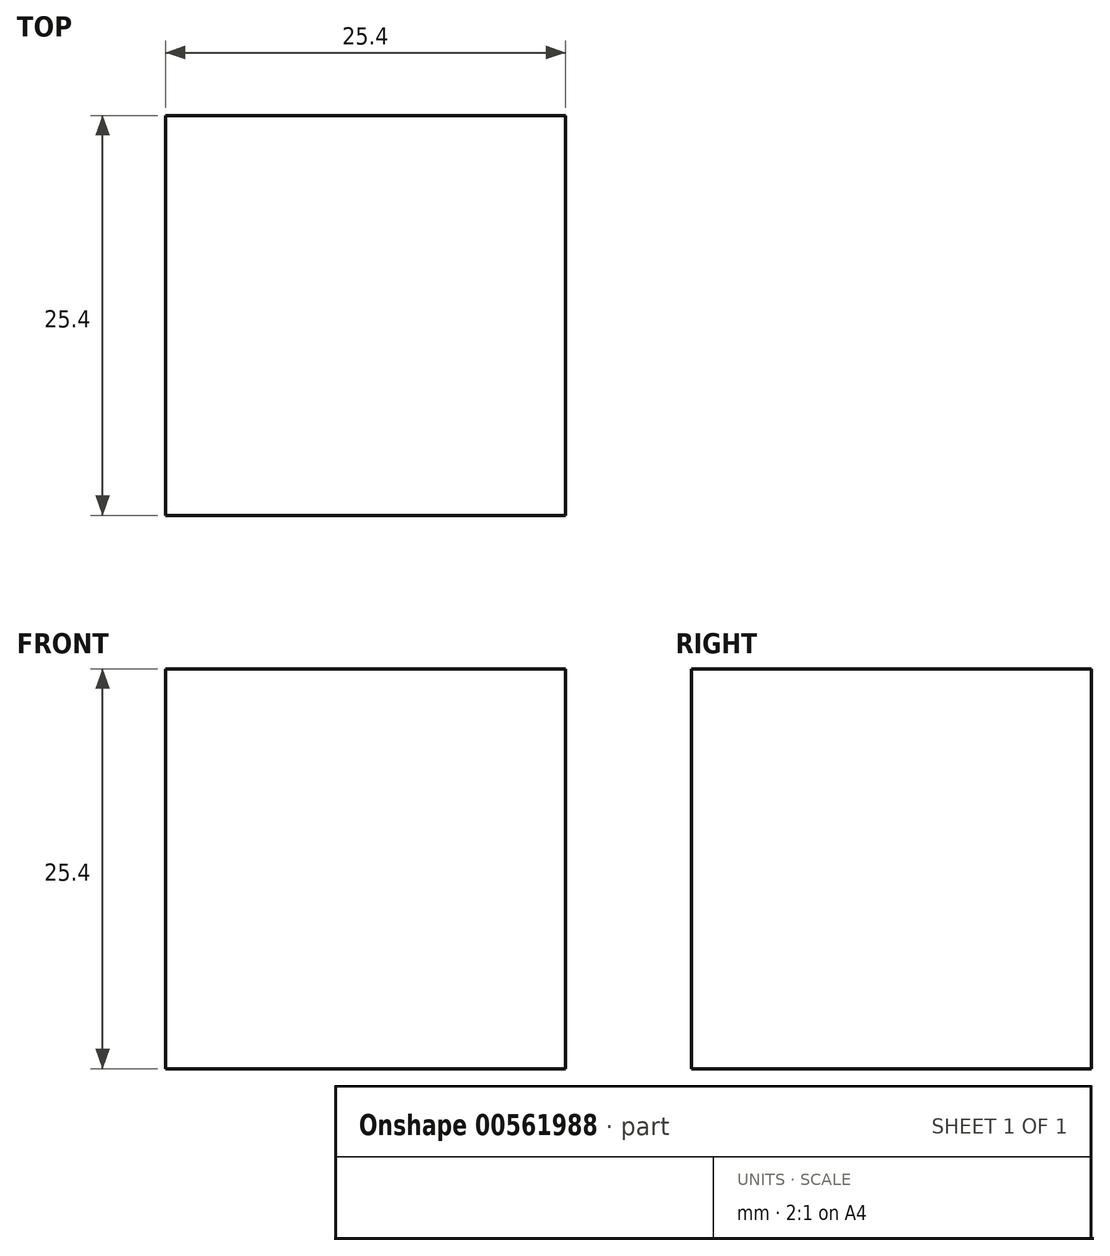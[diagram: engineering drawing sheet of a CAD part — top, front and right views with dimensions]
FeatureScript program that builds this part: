
annotation { "Feature Type Name" : "Feature", "Feature Type Description" : "" }
export const myFeature = defineFeature(function(context is Context, id is Id, definition is map)
    precondition{}
    {
        {
            var Q0;
            Q0=qCreatedBy(makeId("Front.planeOp"),FACE);
            var sketch = newSketch(context, id + "F0", { "sketchPlane" : qUnion([Q0])});
            skLineSegment(sketch, "E0.bottom", {"start": v(-72.33, 30.5) * mm, "end": v(-46.93, 30.5) * mm});
            skLineSegment(sketch, "E0.top", {"start": v(-72.33, 5.1) * mm, "end": v(-46.93, 5.1) * mm});
            skLineSegment(sketch, "E0.left", {"start": v(-72.33, 30.5) * mm, "end": v(-72.33, 5.1) * mm});
            skLineSegment(sketch, "E0.right", {"start": v(-46.93, 30.5) * mm, "end": v(-46.93, 5.1) * mm});
            skSolve(sketch);
        }
        {
            var Q0;
            Q0=makeQuery(id+"F0.imprint","IMPRINT",FACE,{"disambiguationData":[TD([[makeQuery(id+"F0.imprint","IMPRINT",EDGE,{"derivedFrom":sQuery(id+"F0.wireOp",EDGE,"E0.bottom")}),-1.0]])]});
            extrude(context, id + "F1", {"entities" : qUnion([Q0]), "depth" : 25.4 * mm, "offsetDistance" : 25.4 * mm});
        }
    });
